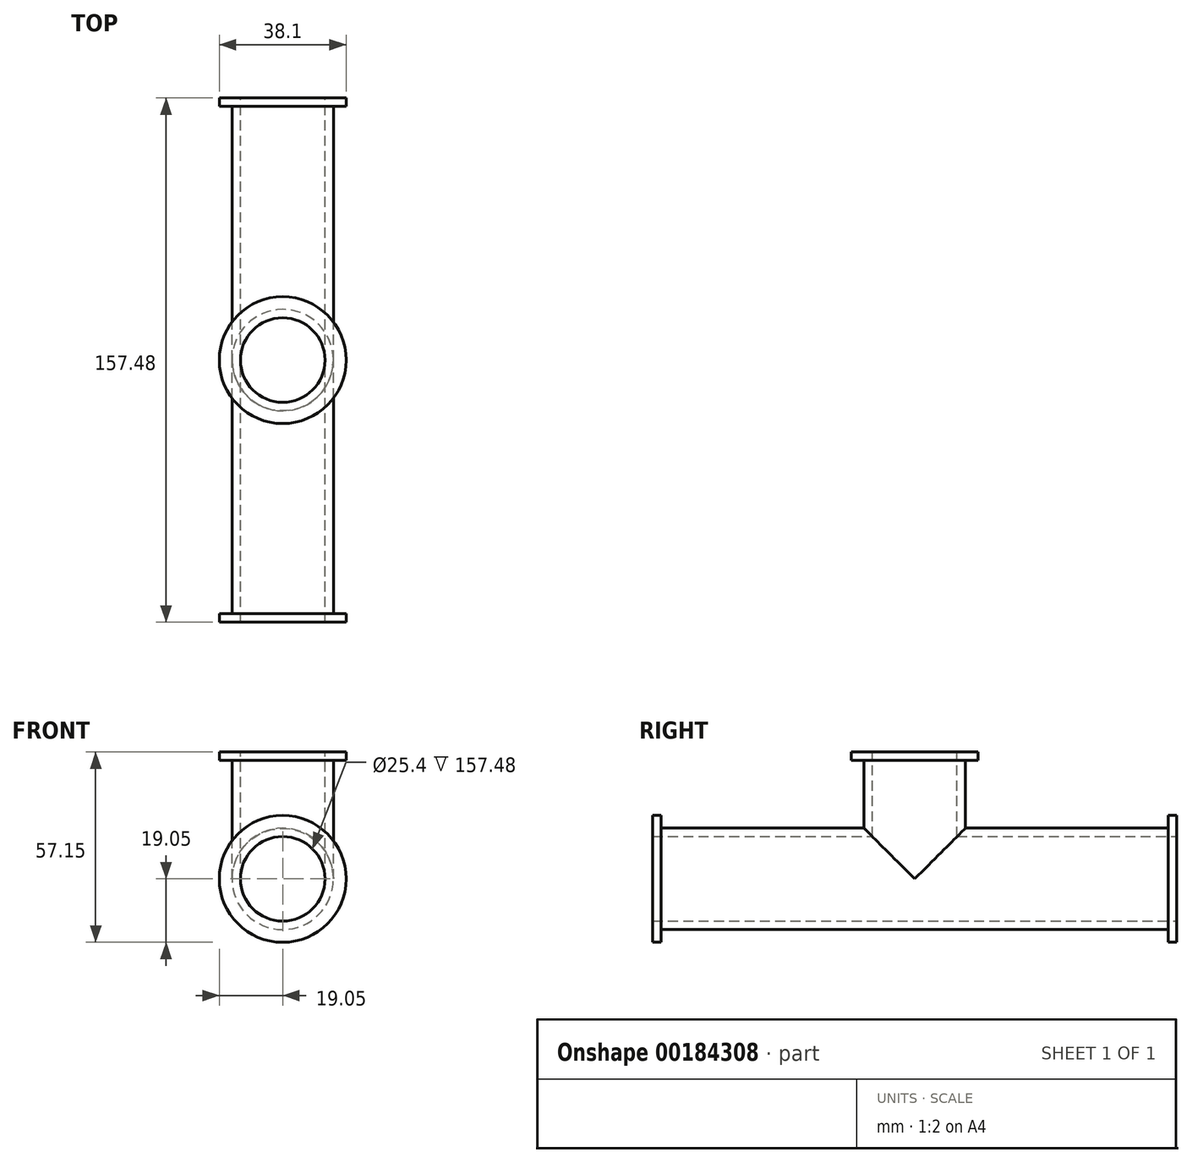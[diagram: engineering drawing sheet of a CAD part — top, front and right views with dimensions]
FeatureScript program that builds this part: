
annotation { "Feature Type Name" : "Feature", "Feature Type Description" : "" }
export const myFeature = defineFeature(function(context is Context, id is Id, definition is map)
    precondition{}
    {
        {
            var Q0;
            Q0=qCreatedBy(makeId("Front.planeOp"),FACE);
            var sketch = newSketch(context, id + "F0", { "sketchPlane" : qUnion([Q0])});
            skCircle(sketch, "E0", {"center": v(0, 0) * mm, "radius": 19.05 * mm});
            skCircle(sketch, "E1", {"center": v(0, 0) * mm, "radius": 12.7 * mm});
            skCircle(sketch, "E2", {"center": v(0, 0) * mm, "radius": 15.24 * mm});
            skSolve(sketch);
        }
        {
            var Q0;
            Q0=makeQuery(id+"F0.imprint","IMPRINT",FACE,{"disambiguationData":[TD([[makeQuery(id+"F0.imprint","IMPRINT",EDGE,{"derivedFrom":sQuery(id+"F0.wireOp",EDGE,"E1")}),-1.0]])]});
            extrude(context, id + "F1", {"entities" : qUnion([Q0]), "depth" : 157.48 * mm});
        }
        {
            var Q0;
            Q0=makeQuery(id+"F0.imprint","IMPRINT",FACE,{"disambiguationData":[TD([[makeQuery(id+"F0.imprint","IMPRINT",EDGE,{"derivedFrom":sQuery(id+"F0.wireOp",EDGE,"E0")}),1.0]])]});
            extrude(context, id + "F2", {"entities" : qUnion([Q0]), "operationType" : NewBodyOperationType.ADD, "depth" : 2.54 * mm});
        }
        {
            var Q0;
            Q0=makeQuery(id+"F1.opExtrude","CAP_FACE",FACE,{"disambiguationData":[OSD([sQuery(id+"F0.wireOp",EDGE,"E1"),sQuery(id+"F0.wireOp",EDGE,"E2")])],"isStart":false});
            var sketch = newSketch(context, id + "F3", { "sketchPlane" : qUnion([Q0])});
            skCircle(sketch, "E3", {"center": v(0, 0) * mm, "radius": 15.24 * mm});
            skCircle(sketch, "E4", {"center": v(0, 0) * mm, "radius": 19.05 * mm});
            skSolve(sketch);
        }
        {
            var Q0;
            Q0 = qSketchRegion(id + "F3", true);
            extrude(context, id + "F4", {"entities" : qUnion([Q0]), "operationType" : NewBodyOperationType.ADD, "oppositeDirection" : true, "depth" : 2.54 * mm});
        }
        {
            var Q0;
            Q0=qCreatedBy(makeId("Top.planeOp"),FACE);
            cPlane(context, id + "F5", {"entities" : qUnion([Q0]), "cplaneType" : CPlaneType.OFFSET, "offset" : 25.4 * mm, "width" : 152.4 * mm, "height" : 152.4 * mm});
        }
        {
            var Q0;
            Q0=qCreatedBy(id+"F5.planeOp",FACE);
            var sketch = newSketch(context, id + "F6", { "sketchPlane" : qUnion([Q0])});
            skLineSegment(sketch, "E5", {"start": v(0, -2.54) * mm, "end": v(0, -78.74) * mm, "construction": true});
            skCircle(sketch, "E6", {"center": v(0, -78.74) * mm, "radius": 19.05 * mm});
            skCircle(sketch, "E7", {"center": v(0, -78.74) * mm, "radius": 15.24 * mm});
            skCircle(sketch, "E8", {"center": v(0, -78.74) * mm, "radius": 12.7 * mm});
            skSolve(sketch);
        }
        {
            var Q0;
            Q0=makeQuery(id+"F6.imprint","IMPRINT",FACE,{"disambiguationData":[TD([[makeQuery(id+"F6.imprint","IMPRINT",EDGE,{"derivedFrom":sQuery(id+"F6.wireOp",EDGE,"E7")}),1.0]])]});
            extrude(context, id + "F7", {"entities" : qUnion([Q0]), "operationType" : NewBodyOperationType.ADD, "oppositeDirection" : true, "depth" : 25.4 * mm, "hasSecondDirection" : true, "secondDirectionOppositeDirection" : false, "secondDirectionDepth" : 12.7 * mm});
        }
        {
            var Q0;
            Q0=makeQuery(id+"F7.opExtrude","CAP_FACE",FACE,{"disambiguationData":[OSD([sQuery(id+"F6.wireOp",EDGE,"E7"),sQuery(id+"F6.wireOp",EDGE,"E8")])],"isStart":true});
            var sketch = newSketch(context, id + "F8", { "sketchPlane" : qUnion([Q0])});
            skCircle(sketch, "E9", {"center": v(0, -78.74) * mm, "radius": 15.24 * mm});
            skCircle(sketch, "E10", {"center": v(0, -78.74) * mm, "radius": 19.05 * mm});
            skSolve(sketch);
        }
        {
            var Q0;
            Q0 = qSketchRegion(id + "F8", true);
            extrude(context, id + "F9", {"entities" : qUnion([Q0]), "operationType" : NewBodyOperationType.ADD, "oppositeDirection" : true, "depth" : 2.54 * mm});
        }
        {
            var Q0;
            Q0=makeQuery(id+"F0.imprint","IMPRINT",FACE,{"disambiguationData":[TD([[makeQuery(id+"F0.imprint","IMPRINT",EDGE,{"derivedFrom":sQuery(id+"F0.wireOp",EDGE,"E1")}),1.0]])]});
            extrude(context, id + "F10", {"entities" : qUnion([Q0]), "operationType" : NewBodyOperationType.REMOVE, "depth" : 101.6 * mm});
        }
        {
            var Q0;
            Q0=makeQuery(id+"F8.imprint","IMPRINT",FACE,{"disambiguationData":[TD([[makeQuery(id+"F8.imprint","IMPRINT",EDGE,{"derivedFrom":makeQuery(id+"F7.opExtrude","CAP_EDGE",EDGE,{"disambiguationData":[OSD([sQuery(id+"F6.wireOp",EDGE,"E8")])],"isStart":true})}),1.0]])]});
            extrude(context, id + "F11", {"entities" : qUnion([Q0]), "operationType" : NewBodyOperationType.REMOVE, "oppositeDirection" : true, "depth" : 38.1 * mm});
        }
    });
